# Revit family: Rectangular-Duct-Endcap-w-KoolDuct-Insulation-System
name_source: partatom
category: Duct Fittings
units: mm (PartAtom-declared; Revit-internal decimal feet)

## family parameters
Always vertical = Yes
Classification Number = 23.75.70.14
Cut with Voids When Loaded = No
Part Type = Cap
Round Connector Dimension = Use Diameter
Shared = No
Work Plane-Based = No

## types (1)
- KoolDuct Duct
    Assembly Code = D3040100
    Construction Details = http://www.arcat.com
    Cost = 0 $
    Default Elevation = 0' - 0"
    Description = Rectangular Duct Endcap w/ KoolDuct Insulation System
    Installation-Fabrication = http://www.trustgreenguard.com
    Insulation Thickness = 2"
    Keynote = 23 07 19
    Length = 1"
    Manufacturer = Kingspan Insulation LLC
    Manufacturer Fax = 678-589-7325
    Manufacturer Website = http://www.trustgreenguard.com
    Model = Rectangular Duct Endcap w/ KoolDuct Insulation
    Product Data = http://www.arcat.com
    Product Properties = http://www.trustgreenguard.com
    Revision = R1_2016-10
    Sales Information = http://www.trustgreenguard.com
    Specification = http://www.arcat.com
    URL = http://www.trustgreenguard.com

## geometry (parser evidence)
native form markers: Sweep x2
no freeform markers — native parametric forms only
